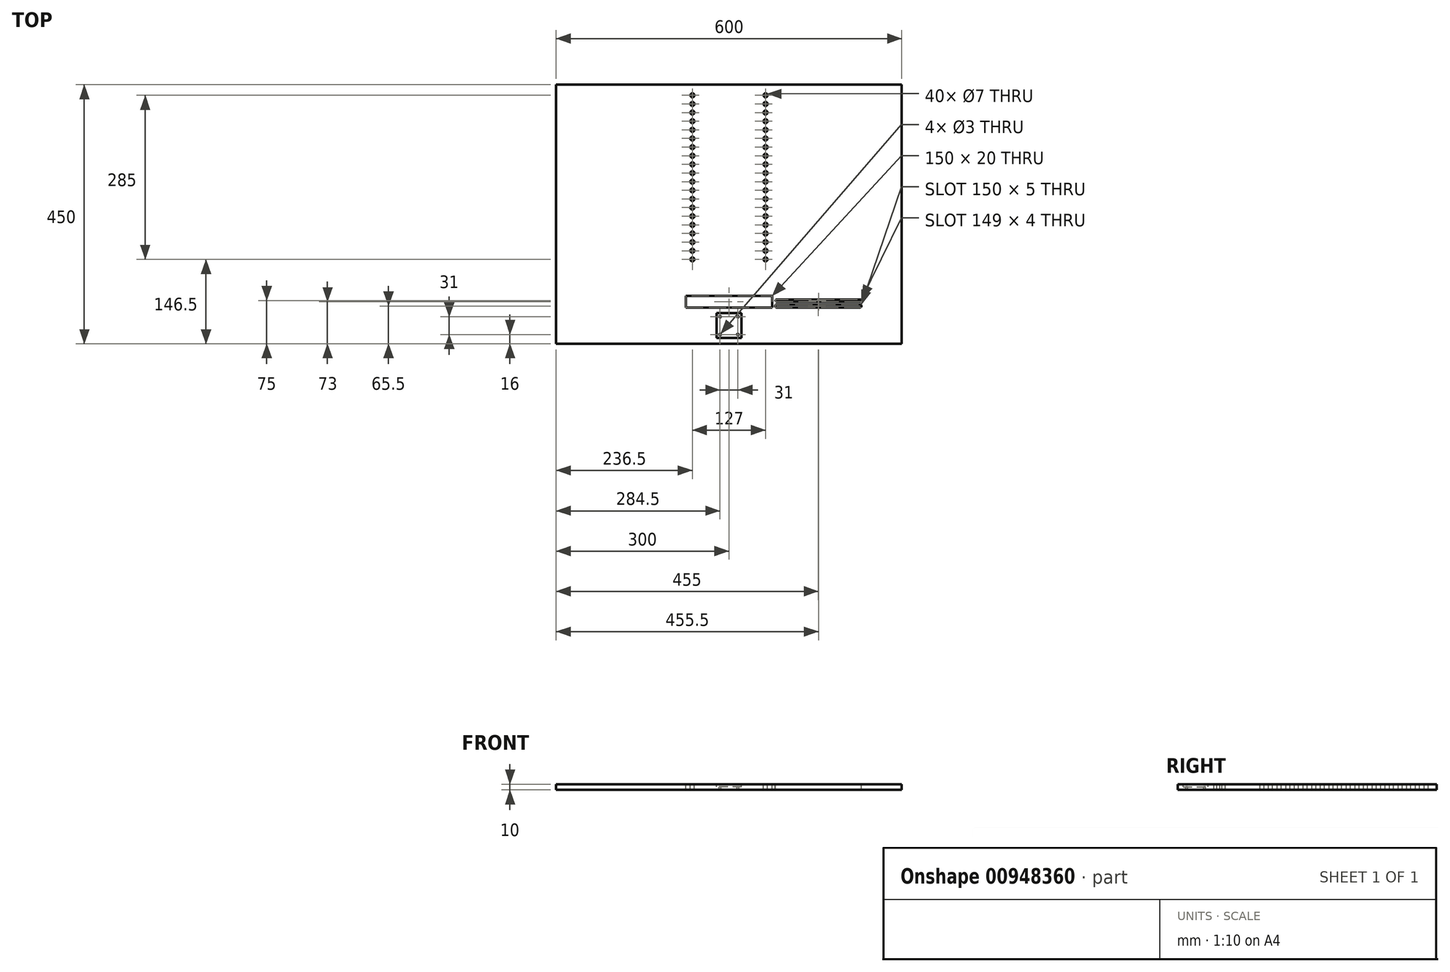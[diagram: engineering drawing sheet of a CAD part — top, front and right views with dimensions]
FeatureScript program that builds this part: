
annotation { "Feature Type Name" : "Feature", "Feature Type Description" : "" }
export const myFeature = defineFeature(function(context is Context, id is Id, definition is map)
    precondition{}
    {
        {
            var Q0;
            Q0=qCreatedBy(makeId("Top.planeOp"),FACE);
            var sketch = newSketch(context, id + "F0", { "sketchPlane" : qUnion([Q0])});
            skLineSegment(sketch, "E0.bottom", {"start": v(300, -225) * mm, "end": v(-300, -225) * mm});
            skLineSegment(sketch, "E0.top", {"start": v(300, 225) * mm, "end": v(-300, 225) * mm});
            skLineSegment(sketch, "E0.left", {"start": v(300, -225) * mm, "end": v(300, 225) * mm});
            skLineSegment(sketch, "E0.right", {"start": v(-300, -225) * mm, "end": v(-300, 225) * mm});
            skPoint(sketch, "E0.middle", {"position": v(0, 0) * mm});
            skSolve(sketch);
        }
        {
            var Q0;
            Q0 = qSketchRegion(id + "F0", true);
            extrude(context, id + "F1", {"entities" : qUnion([Q0]), "depth" : 10 * mm, "offsetDistance" : 25 * mm});
        }
        {
            var Q0;
            Q0=makeQuery(id+"F1.opExtrude","CAP_FACE",FACE,{"disambiguationData":[OSD([sQuery(id+"F0.wireOp",EDGE,"E0.bottom"),sQuery(id+"F0.wireOp",EDGE,"E0.top"),sQuery(id+"F0.wireOp",EDGE,"E0.left"),sQuery(id+"F0.wireOp",EDGE,"E0.right")])],"isStart":false});
            var sketch = newSketch(context, id + "F2", { "sketchPlane" : qUnion([Q0])});
            skLineSegment(sketch, "E1", {"start": v(0, 225) * mm, "end": v(0, -225) * mm, "construction": true});
            skCircle(sketch, "E2", {"center": v(-63.5, 206.5) * mm, "radius": 3.5 * mm});
            skCircle(sketch, "E3.0.1.0", {"center": v(-63.5, 191.5) * mm, "radius": 3.5 * mm});
            skCircle(sketch, "E3.0.2.0", {"center": v(-63.5, 176.5) * mm, "radius": 3.5 * mm});
            skCircle(sketch, "E3.0.3.0", {"center": v(-63.5, 161.5) * mm, "radius": 3.5 * mm});
            skCircle(sketch, "E3.0.4.0", {"center": v(-63.5, 146.5) * mm, "radius": 3.5 * mm});
            skCircle(sketch, "E3.0.5.0", {"center": v(-63.5, 131.5) * mm, "radius": 3.5 * mm});
            skCircle(sketch, "E3.0.6.0", {"center": v(-63.5, 116.5) * mm, "radius": 3.5 * mm});
            skCircle(sketch, "E3.0.7.0", {"center": v(-63.5, 101.5) * mm, "radius": 3.5 * mm});
            skCircle(sketch, "E3.0.8.0", {"center": v(-63.5, 86.5) * mm, "radius": 3.5 * mm});
            skCircle(sketch, "E3.0.9.0", {"center": v(-63.5, 71.5) * mm, "radius": 3.5 * mm});
            skCircle(sketch, "E3.0.10.0", {"center": v(-63.5, 56.5) * mm, "radius": 3.5 * mm});
            skCircle(sketch, "E3.0.11.0", {"center": v(-63.5, 41.5) * mm, "radius": 3.5 * mm});
            skCircle(sketch, "E3.0.12.0", {"center": v(-63.5, 26.5) * mm, "radius": 3.5 * mm});
            skCircle(sketch, "E3.0.13.0", {"center": v(-63.5, 11.5) * mm, "radius": 3.5 * mm});
            skCircle(sketch, "E3.0.14.0", {"center": v(-63.5, -3.5) * mm, "radius": 3.5 * mm});
            skCircle(sketch, "E3.0.15.0", {"center": v(-63.5, -18.5) * mm, "radius": 3.5 * mm});
            skCircle(sketch, "E3.0.16.0", {"center": v(-63.5, -33.5) * mm, "radius": 3.5 * mm});
            skCircle(sketch, "E3.0.17.0", {"center": v(-63.5, -48.5) * mm, "radius": 3.5 * mm});
            skCircle(sketch, "E3.0.18.0", {"center": v(-63.5, -63.5) * mm, "radius": 3.5 * mm});
            skCircle(sketch, "E3.0.19.0", {"center": v(-63.5, -78.5) * mm, "radius": 3.5 * mm});
            skLineSegment(sketch, "E3.direction2", {"start": v(-63.5, 206.5) * mm, "end": v(-63.5, 191.5) * mm, "construction": true});
            skCircle(sketch, "E4.MirrorC", {"center": v(63.5, 191.5) * mm, "radius": 3.5 * mm});
            skCircle(sketch, "E5.MirrorC", {"center": v(63.5, 86.5) * mm, "radius": 3.5 * mm});
            skCircle(sketch, "E6.MirrorC", {"center": v(63.5, 41.5) * mm, "radius": 3.5 * mm});
            skCircle(sketch, "E7.MirrorC", {"center": v(63.5, 26.5) * mm, "radius": 3.5 * mm});
            skCircle(sketch, "E8.MirrorC", {"center": v(63.5, 101.5) * mm, "radius": 3.5 * mm});
            skCircle(sketch, "E9.MirrorC", {"center": v(63.5, -18.5) * mm, "radius": 3.5 * mm});
            skCircle(sketch, "E10.MirrorC", {"center": v(63.5, 131.5) * mm, "radius": 3.5 * mm});
            skCircle(sketch, "E11.MirrorC", {"center": v(63.5, -63.5) * mm, "radius": 3.5 * mm});
            skCircle(sketch, "E12.MirrorC", {"center": v(63.5, 71.5) * mm, "radius": 3.5 * mm});
            skCircle(sketch, "E13.MirrorC", {"center": v(63.5, 161.5) * mm, "radius": 3.5 * mm});
            skCircle(sketch, "E14.MirrorC", {"center": v(63.5, 176.5) * mm, "radius": 3.5 * mm});
            skCircle(sketch, "E15.MirrorC", {"center": v(63.5, -48.5) * mm, "radius": 3.5 * mm});
            skCircle(sketch, "E16.MirrorC", {"center": v(63.5, 11.5) * mm, "radius": 3.5 * mm});
            skCircle(sketch, "E17.MirrorC", {"center": v(63.5, -78.5) * mm, "radius": 3.5 * mm});
            skCircle(sketch, "E18.MirrorC", {"center": v(63.5, -33.5) * mm, "radius": 3.5 * mm});
            skCircle(sketch, "E19.MirrorC", {"center": v(63.5, 146.5) * mm, "radius": 3.5 * mm});
            skCircle(sketch, "E20.MirrorC", {"center": v(63.5, -3.5) * mm, "radius": 3.5 * mm});
            skCircle(sketch, "E21.MirrorC", {"center": v(63.5, 116.5) * mm, "radius": 3.5 * mm});
            skCircle(sketch, "E22.MirrorC", {"center": v(63.5, 56.5) * mm, "radius": 3.5 * mm});
            skCircle(sketch, "E23.MirrorC", {"center": v(63.5, 206.5) * mm, "radius": 3.5 * mm});
            skSolve(sketch);
        }
        {
            var Q0;
            Q0 = qSketchRegion(id + "F2", true);
            extrude(context, id + "F3", {"entities" : qUnion([Q0]), "operationType" : NewBodyOperationType.REMOVE, "oppositeDirection" : true, "depth" : 10 * mm, "offsetDistance" : 25 * mm});
        }
        {
            var Q0;
            Q0=makeQuery(id+"F1.opExtrude","CAP_FACE",FACE,{"disambiguationData":[OSD([sQuery(id+"F0.wireOp",EDGE,"E0.bottom"),sQuery(id+"F0.wireOp",EDGE,"E0.top"),sQuery(id+"F0.wireOp",EDGE,"E0.left"),sQuery(id+"F0.wireOp",EDGE,"E0.right")])],"isStart":false});
            var sketch = newSketch(context, id + "F4", { "sketchPlane" : qUnion([Q0])});
            skLineSegment(sketch, "E24", {"start": v(0, 225) * mm, "end": v(0, -225) * mm, "construction": true});
            skLineSegment(sketch, "E25.bottom", {"start": v(75, -142) * mm, "end": v(-75, -142) * mm});
            skLineSegment(sketch, "E25.top", {"start": v(75, -162) * mm, "end": v(-75, -162) * mm});
            skLineSegment(sketch, "E25.left", {"start": v(75, -142) * mm, "end": v(75, -162) * mm});
            skLineSegment(sketch, "E25.right", {"start": v(-75, -142) * mm, "end": v(-75, -162) * mm});
            skPoint(sketch, "E25.middle", {"position": v(0, -152) * mm});
            skLineSegment(sketch, "E26.bottom", {"start": v(21.5, -215) * mm, "end": v(-21.5, -215) * mm});
            skLineSegment(sketch, "E26.top", {"start": v(21.5, -172) * mm, "end": v(-21.5, -172) * mm});
            skLineSegment(sketch, "E26.left", {"start": v(21.5, -215) * mm, "end": v(21.5, -172) * mm});
            skLineSegment(sketch, "E26.right", {"start": v(-21.5, -215) * mm, "end": v(-21.5, -172) * mm});
            skPoint(sketch, "E26.middle", {"position": v(0, -193.5) * mm});
            skCircle(sketch, "E27", {"center": v(-15.5, -178) * mm, "radius": 1.5 * mm});
            skCircle(sketch, "E28", {"center": v(15.5, -178) * mm, "radius": 1.5 * mm});
            skCircle(sketch, "E29", {"center": v(15.5, -209) * mm, "radius": 1.5 * mm});
            skCircle(sketch, "E30", {"center": v(-15.5, -209) * mm, "radius": 1.5 * mm});
            skLineSegment(sketch, "E31", {"start": v(300, -152) * mm, "end": v(-300, -152) * mm, "construction": true});
            skLineSegment(sketch, "E32.bottom", {"start": v(82.5, -157) * mm, "end": v(227.5, -157) * mm});
            skLineSegment(sketch, "E32.top", {"start": v(82.5, -162) * mm, "end": v(227.5, -162) * mm});
            skLineSegment(sketch, "E33.bottom", {"start": v(83, -152) * mm, "end": v(228, -152) * mm});
            skLineSegment(sketch, "E33.top", {"start": v(83, -148) * mm, "end": v(228, -148) * mm});
            skArc(sketch, "E34", {"start": v(83, -148) * mm, "mid": v(81, -150) * mm, "end": v(83, -152) * mm});
            skArc(sketch, "E35", {"start": v(228, -152) * mm, "mid": v(230, -150) * mm, "end": v(228, -148) * mm});
            skArc(sketch, "E36", {"start": v(82.5, -157) * mm, "mid": v(80, -159.5) * mm, "end": v(82.5, -162) * mm});
            skArc(sketch, "E37", {"start": v(227.5, -162) * mm, "mid": v(230, -159.5) * mm, "end": v(227.5, -157) * mm});
            skSolve(sketch);
        }
        {
            var Q0;
            Q0=makeQuery(id+"F4.imprint","IMPRINT",FACE,{"disambiguationData":[TD([[makeQuery(id+"F4.imprint","IMPRINT",EDGE,{"derivedFrom":sQuery(id+"F4.wireOp",EDGE,"E26.bottom")}),-1.0]])]});
            extrude(context, id + "F5", {"entities" : qUnion([Q0]), "operationType" : NewBodyOperationType.REMOVE, "oppositeDirection" : true, "depth" : 5 * mm, "offsetDistance" : 25 * mm});
        }
        {
            var Q0;
            Q0=makeQuery(id+"F5.boolean.opBoolean","SPLIT",FACE,{"disambiguationData":[TD([makeQuery(id+"F5.opExtrude","SWEPT_FACE",FACE,{"disambiguationData":[OSD([sQuery(id+"F4.wireOp",EDGE,"E29")])]})])],"derivedFrom":makeQuery(id+"F1.opExtrude","CAP_FACE",FACE,{"disambiguationData":[OSD([sQuery(id+"F0.wireOp",EDGE,"E0.bottom"),sQuery(id+"F0.wireOp",EDGE,"E0.top"),sQuery(id+"F0.wireOp",EDGE,"E0.left"),sQuery(id+"F0.wireOp",EDGE,"E0.right")])],"isStart":false})});
            var Q1;
            Q1=makeQuery(id+"F5.boolean.opBoolean","SPLIT",FACE,{"disambiguationData":[TD([makeQuery(id+"F5.opExtrude","SWEPT_FACE",FACE,{"disambiguationData":[OSD([sQuery(id+"F4.wireOp",EDGE,"E28")])]})])],"derivedFrom":makeQuery(id+"F1.opExtrude","CAP_FACE",FACE,{"disambiguationData":[OSD([sQuery(id+"F0.wireOp",EDGE,"E0.bottom"),sQuery(id+"F0.wireOp",EDGE,"E0.top"),sQuery(id+"F0.wireOp",EDGE,"E0.left"),sQuery(id+"F0.wireOp",EDGE,"E0.right")])],"isStart":false})});
            var Q2;
            Q2=makeQuery(id+"F5.boolean.opBoolean","SPLIT",FACE,{"disambiguationData":[TD([makeQuery(id+"F5.opExtrude","SWEPT_FACE",FACE,{"disambiguationData":[OSD([sQuery(id+"F4.wireOp",EDGE,"E27")])]})])],"derivedFrom":makeQuery(id+"F1.opExtrude","CAP_FACE",FACE,{"disambiguationData":[OSD([sQuery(id+"F0.wireOp",EDGE,"E0.bottom"),sQuery(id+"F0.wireOp",EDGE,"E0.top"),sQuery(id+"F0.wireOp",EDGE,"E0.left"),sQuery(id+"F0.wireOp",EDGE,"E0.right")])],"isStart":false})});
            var Q3;
            Q3=makeQuery(id+"F5.boolean.opBoolean","SPLIT",FACE,{"disambiguationData":[TD([makeQuery(id+"F5.opExtrude","SWEPT_FACE",FACE,{"disambiguationData":[OSD([sQuery(id+"F4.wireOp",EDGE,"E30")])]})])],"derivedFrom":makeQuery(id+"F1.opExtrude","CAP_FACE",FACE,{"disambiguationData":[OSD([sQuery(id+"F0.wireOp",EDGE,"E0.bottom"),sQuery(id+"F0.wireOp",EDGE,"E0.top"),sQuery(id+"F0.wireOp",EDGE,"E0.left"),sQuery(id+"F0.wireOp",EDGE,"E0.right")])],"isStart":false})});
            extrude(context, id + "F6", {"entities" : qUnion([Q0, Q1, Q2, Q3]), "operationType" : NewBodyOperationType.REMOVE, "oppositeDirection" : true, "depth" : 10 * mm, "offsetDistance" : 25 * mm});
        }
        {
            var Q0;
            Q0=makeQuery(id+"F4.imprint","IMPRINT",FACE,{"disambiguationData":[TD([[makeQuery(id+"F4.imprint","IMPRINT",EDGE,{"derivedFrom":sQuery(id+"F4.wireOp",EDGE,"E25.bottom")}),1.0]])]});
            extrude(context, id + "F7", {"entities" : qUnion([Q0]), "operationType" : NewBodyOperationType.REMOVE, "oppositeDirection" : true, "depth" : 10 * mm, "offsetDistance" : 25 * mm});
        }
        {
            var Q0;
            Q0=makeQuery(id+"F4.imprint","IMPRINT",FACE,{"disambiguationData":[TD([[makeQuery(id+"F4.imprint","IMPRINT",EDGE,{"derivedFrom":sQuery(id+"F4.wireOp",EDGE,"E32.bottom")}),-1.0]])]});
            extrude(context, id + "F8", {"entities" : qUnion([Q0]), "operationType" : NewBodyOperationType.REMOVE, "oppositeDirection" : true, "depth" : 10 * mm, "offsetDistance" : 25 * mm});
        }
        {
            var Q0;
            Q0=makeQuery(id+"F4.imprint","IMPRINT",FACE,{"disambiguationData":[TD([[makeQuery(id+"F4.imprint","IMPRINT",EDGE,{"derivedFrom":sQuery(id+"F4.wireOp",EDGE,"E33.bottom")}),1.0]])]});
            extrude(context, id + "F9", {"entities" : qUnion([Q0]), "operationType" : NewBodyOperationType.REMOVE, "oppositeDirection" : true, "depth" : 10 * mm, "offsetDistance" : 25 * mm});
        }
        {
            var Q0;
            Q0 = qSketchRegion(id + "F2", true);
            extrude(context, id + "F10", {"entities" : qUnion([Q0]), "operationType" : NewBodyOperationType.REMOVE, "oppositeDirection" : true, "depth" : 10 * mm, "offsetDistance" : 25 * mm});
        }
    });
